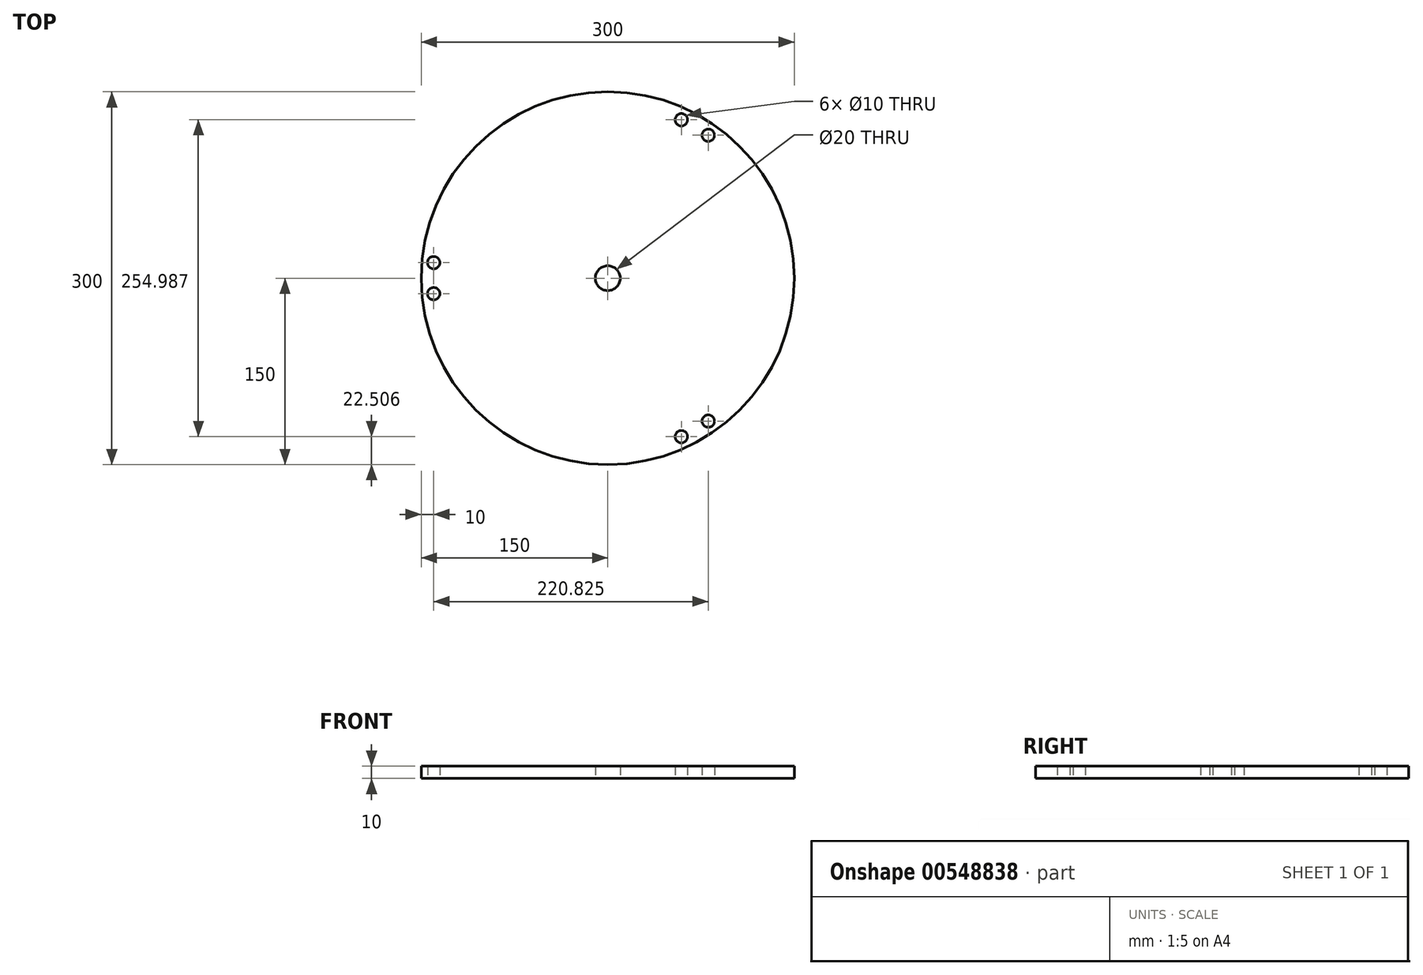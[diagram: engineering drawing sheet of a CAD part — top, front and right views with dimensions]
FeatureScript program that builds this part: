
annotation { "Feature Type Name" : "Feature", "Feature Type Description" : "" }
export const myFeature = defineFeature(function(context is Context, id is Id, definition is map)
    precondition{}
    {
        {
            var Q0;
            Q0=qCreatedBy(makeId("Top.planeOp"),FACE);
            var sketch = newSketch(context, id + "F0", { "sketchPlane" : qUnion([Q0])});
            skCircle(sketch, "E0", {"center": v(0, 0) * mm, "radius": 150 * mm});
            skLineSegment(sketch, "E1", {"start": v(0, 0) * mm, "end": v(-150, 0) * mm, "construction": true});
            skLineSegment(sketch, "E2", {"start": v(0, 0) * mm, "end": v(75, -129.9) * mm, "construction": true});
            skLineSegment(sketch, "E3", {"start": v(0, 0) * mm, "end": v(75, 129.9) * mm, "construction": true});
            skCircle(sketch, "E4", {"center": v(-140, 12.5) * mm, "radius": 5 * mm});
            skCircle(sketch, "E5", {"center": v(-140, -12.5) * mm, "radius": 5 * mm});
            skCircle(sketch, "E6", {"center": v(59.17, 127.5) * mm, "radius": 5 * mm});
            skCircle(sketch, "E7", {"center": v(80.83, 115) * mm, "radius": 5 * mm});
            skCircle(sketch, "E8", {"center": v(80.83, -115) * mm, "radius": 5 * mm});
            skCircle(sketch, "E9", {"center": v(59.17, -127.5) * mm, "radius": 5 * mm});
            skLineSegment(sketch, "E10", {"start": v(-140, 12.5) * mm, "end": v(-140, -12.5) * mm, "construction": true});
            skLineSegment(sketch, "E11", {"start": v(59.17, 127.5) * mm, "end": v(80.83, 115) * mm, "construction": true});
            skLineSegment(sketch, "E12", {"start": v(80.83, -115) * mm, "end": v(59.17, -127.5) * mm, "construction": true});
            skLineSegment(sketch, "E13", {"start": v(-140, 0) * mm, "end": v(0, 0) * mm, "construction": true});
            skLineSegment(sketch, "E14", {"start": v(70, 121.24) * mm, "end": v(0, 0) * mm, "construction": true});
            skLineSegment(sketch, "E15", {"start": v(70, -121.24) * mm, "end": v(0, 0) * mm, "construction": true});
            skCircle(sketch, "E16", {"center": v(0, 0) * mm, "radius": 10 * mm});
            skSolve(sketch);
        }
        {
            var Q0;
            Q0=qSketchRegion(id+"F0",true);
            extrude(context, id + "F1", {"entities" : qUnion([Q0]), "depth" : 10 * mm, "offsetDistance" : 25 * mm});
        }
    });
